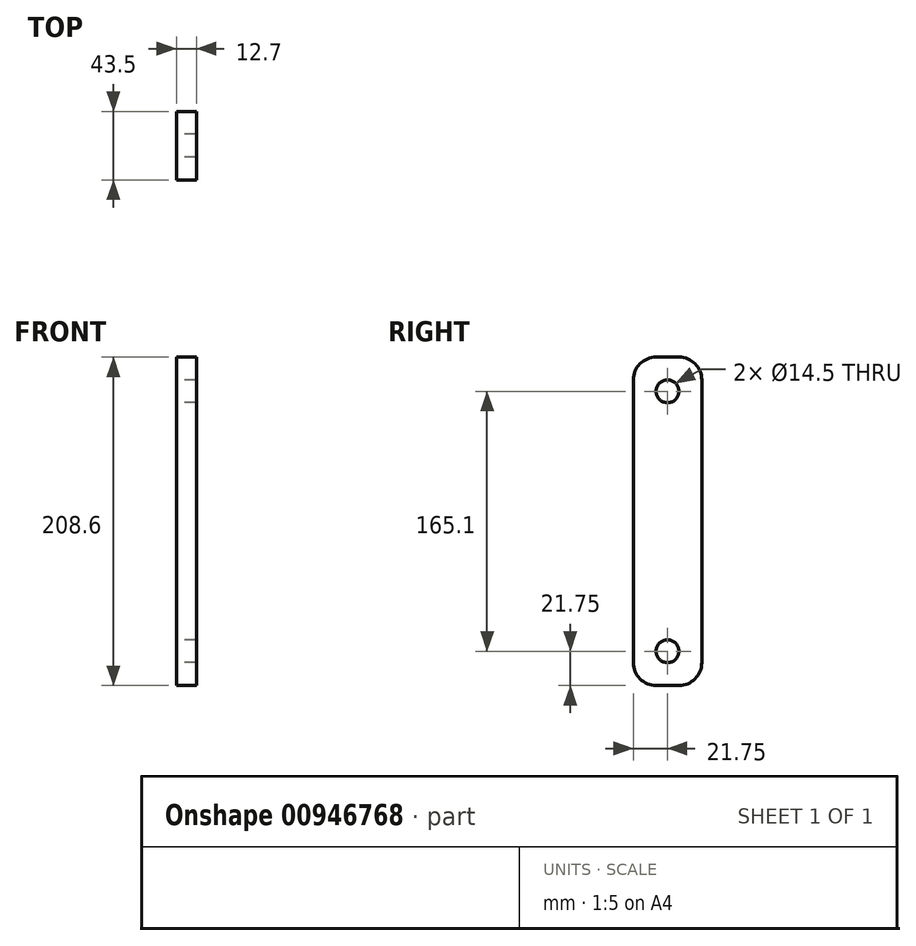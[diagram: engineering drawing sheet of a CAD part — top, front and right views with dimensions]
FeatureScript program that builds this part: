
annotation { "Feature Type Name" : "Feature", "Feature Type Description" : "" }
export const myFeature = defineFeature(function(context is Context, id is Id, definition is map)
    precondition{}
    {
        {
            var Q0;
            Q0=qCreatedBy(makeId("Right.planeOp"),FACE);
            var sketch = newSketch(context, id + "F0", { "sketchPlane" : qUnion([Q0])});
            skCircle(sketch, "E0", {"center": v(0, 0) * mm, "radius": 7.25 * mm});
            skCircle(sketch, "E1", {"center": v(0, -165.1) * mm, "radius": 7.25 * mm});
            skLineSegment(sketch, "E2.bottom", {"start": v(-7.25, 21.75) * mm, "end": v(7.25, 21.75) * mm});
            skLineSegment(sketch, "E2.top", {"start": v(-7.25, -186.85) * mm, "end": v(7.25, -186.85) * mm});
            skLineSegment(sketch, "E2.left", {"start": v(-21.75, 7.25) * mm, "end": v(-21.75, -172.35) * mm});
            skLineSegment(sketch, "E2.right", {"start": v(21.75, 7.25) * mm, "end": v(21.75, -172.35) * mm});
            skPoint(sketch, "E3.visualSharp", {"position": v(-21.75, 21.75) * mm});
            skArc(sketch, "E3.filletArc", {"start": v(-7.25, 21.75) * mm, "mid": v(-17.5, 17.5) * mm, "end": v(-21.75, 7.25) * mm});
            skPoint(sketch, "E4.visualSharp", {"position": v(21.75, 21.75) * mm});
            skArc(sketch, "E4.filletArc", {"start": v(21.75, 7.25) * mm, "mid": v(17.5, 17.5) * mm, "end": v(7.25, 21.75) * mm});
            skPoint(sketch, "E5.visualSharp", {"position": v(21.75, -186.85) * mm});
            skArc(sketch, "E5.filletArc", {"start": v(7.25, -186.85) * mm, "mid": v(17.5, -182.6) * mm, "end": v(21.75, -172.35) * mm});
            skPoint(sketch, "E6.visualSharp", {"position": v(-21.75, -186.85) * mm});
            skArc(sketch, "E6.filletArc", {"start": v(-21.75, -172.35) * mm, "mid": v(-17.5, -182.6) * mm, "end": v(-7.25, -186.85) * mm});
            skSolve(sketch);
        }
        {
            var Q0;
            Q0=makeQuery(id+"F0.imprint","IMPRINT",FACE,{"disambiguationData":[TD([[makeQuery(id+"F0.imprint","IMPRINT",EDGE,{"derivedFrom":sQuery(id+"F0.wireOp",EDGE,"E0")}),-1.0]])]});
            extrude(context, id + "F1", {"entities" : qUnion([Q0]), "depth" : 12.7 * mm, "offsetDistance" : 25.4 * mm});
        }
    });
